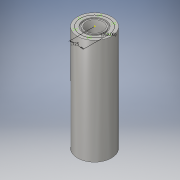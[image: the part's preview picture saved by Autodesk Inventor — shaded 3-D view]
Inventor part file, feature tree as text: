
AUTODESK INVENTOR PART (.ipt)
format: ipt  version: 2016 (Build 200138000, 138)  size: 135,168 bytes
history: native  units: in
note: dims shown in document units (in); Inventor stores cm internally (conversion verified against a paired STEP export)
features: sketch x7, extrude x6
ambient origin geometry x8: Origin, YZ Plane, XZ Plane, XY Plane, X Axis, Y Axis, Z Axis, Center Point
bodies: Solid1 (feature_tree)
feature tree (13):
  extrude  "Extrusion1"  Depth=12.013in TaperAngle=0.0deg
  extrude  "Extrusion2"  Depth=0.995in
  sketch  "Sketch3"  dims[d5=0.071in d6=0.0in d7=0.0666in]
  extrude  "Extrusion3"  Depth=0.071in
  extrude  "Extrusion4"  Depth=14.0in TaperAngle=0.0deg
  extrude  "Extrusion5"  Depth=1.748in
  extrude  "Extrusion6"  Depth=6.588in TaperAngle=0.0deg
  sketch  "Sketch8"  dims[d19=0.725in d20=2.3622in d22=360.0deg]
  sketch  "Sketch1"  dims[d0=1.748in d1=12.013in d2=0.0in]
  sketch  "Sketch2"  dims[d3=1.138in d4=0.995in]
  sketch  "Sketch5"  dims[d9=0.577in d10=-0.1168in d11=14.0in d12=0.0in]
  sketch  "Sketch6"  dims[d13=1.5in d14=1.748in]
  sketch  "Sketch7"  dims[d15=11.435in d16=0.0in d17=6.588in d18=0.0in]
